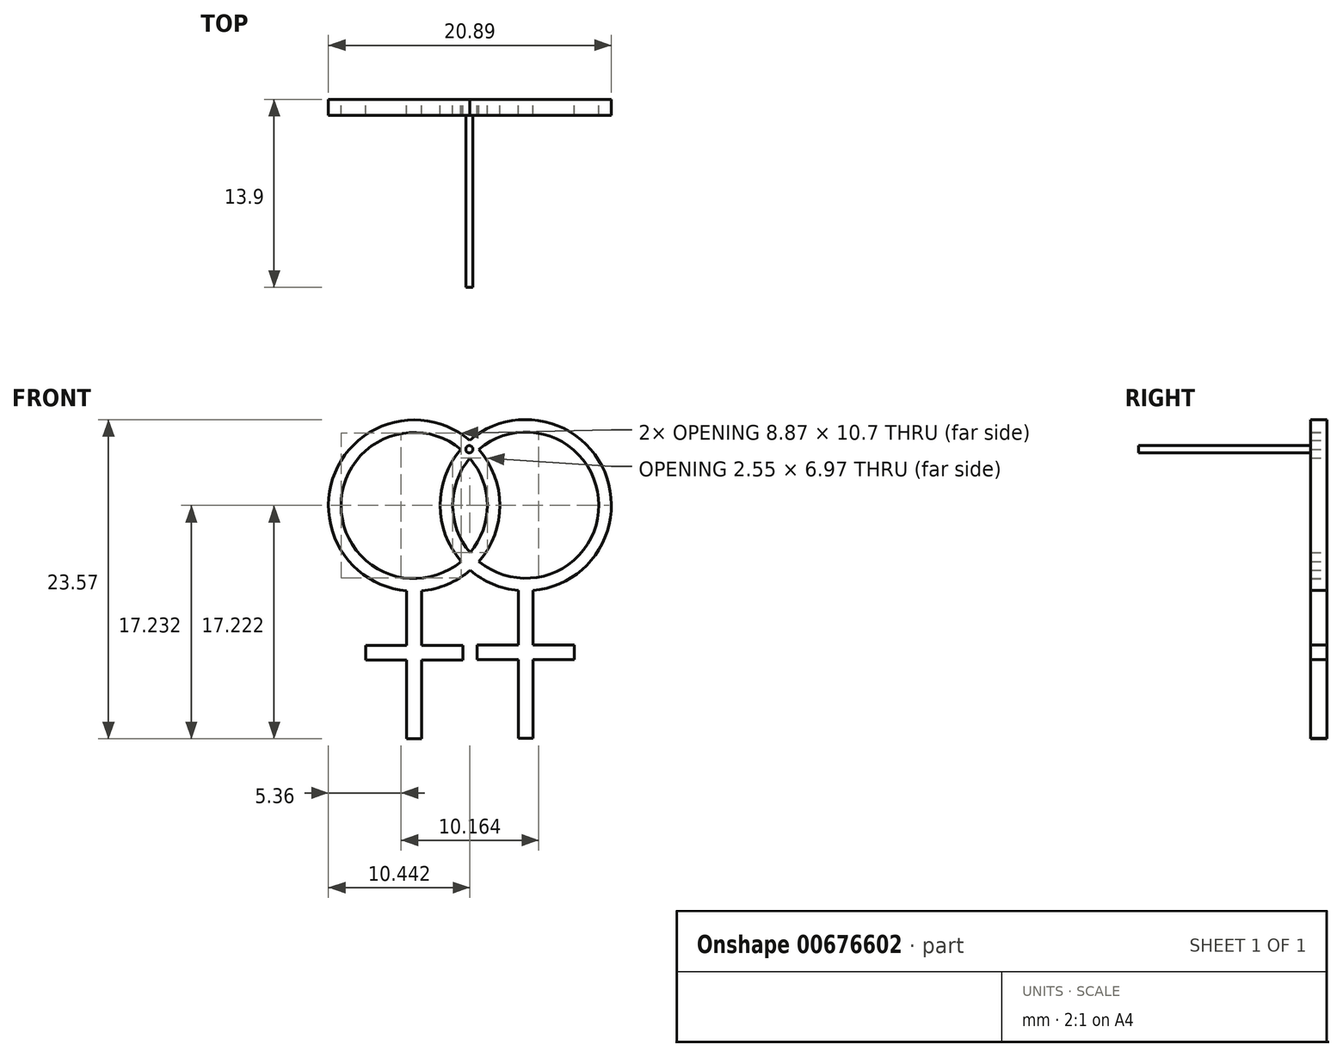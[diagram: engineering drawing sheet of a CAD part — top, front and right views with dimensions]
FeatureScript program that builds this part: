
annotation { "Feature Type Name" : "Feature", "Feature Type Description" : "" }
export const myFeature = defineFeature(function(context is Context, id is Id, definition is map)
    precondition{}
    {
        {
            var Q0;
            Q0=qCreatedBy(makeId("Front.planeOp"),FACE);
            var sketch = newSketch(context, id + "F0", { "sketchPlane" : qUnion([Q0])});
            skArc(sketch, "E0", {"start": v(-22.56, 17.55) * mm, "mid": v(-20.65, 18.03) * mm, "end": v(-18.97, 19.07) * mm});
            skArc(sketch, "E1", {"start": v(-19.66, 28) * mm, "mid": v(-28.5, 23.83) * mm, "end": v(-19.63, 19.72) * mm});
            skLineSegment(sketch, "E2", {"start": v(-23.66, 12.43) * mm, "end": v(-23.66, 6.63) * mm});
            skLineSegment(sketch, "E3", {"start": v(-22.56, 12.43) * mm, "end": v(-22.56, 6.63) * mm});
            skLineSegment(sketch, "E4", {"start": v(-23.66, 6.63) * mm, "end": v(-22.56, 6.63) * mm});
            skPoint(sketch, "E5.orphan", {"position": v(-22.91, 6.63) * mm});
            skPoint(sketch, "E6.start.orphan", {"position": v(-23.1, 30.17) * mm});
            skPoint(sketch, "E7.oppositeSnap0", {"position": v(-22.56, 12.43) * mm});
            skPoint(sketch, "E7.right.end.orphan", {"position": v(-17.65, 12.43) * mm});
            skLineSegment(sketch, "E8", {"start": v(-23.66, 17.55) * mm, "end": v(-23.66, 13.53) * mm});
            skLineSegment(sketch, "E9", {"start": v(-23.66, 13.53) * mm, "end": v(-26.7, 13.53) * mm});
            skLineSegment(sketch, "E10", {"start": v(-26.7, 13.53) * mm, "end": v(-26.7, 12.43) * mm});
            skLineSegment(sketch, "E11", {"start": v(-26.7, 12.43) * mm, "end": v(-23.66, 12.43) * mm});
            skLineSegment(sketch, "E12", {"start": v(-22.56, 17.55) * mm, "end": v(-22.56, 13.53) * mm});
            skLineSegment(sketch, "E13", {"start": v(-22.56, 13.53) * mm, "end": v(-19.52, 13.53) * mm});
            skLineSegment(sketch, "E14", {"start": v(-19.52, 13.53) * mm, "end": v(-19.52, 12.43) * mm});
            skLineSegment(sketch, "E15", {"start": v(-19.52, 12.43) * mm, "end": v(-22.56, 12.43) * mm});
            skArc(sketch, "E16", {"start": v(-14.32, 17.58) * mm, "mid": v(-9.04, 26.34) * mm, "end": v(-19, 28.66) * mm});
            skArc(sketch, "E17", {"start": v(-19, 27.35) * mm, "mid": v(-20.26, 23.86) * mm, "end": v(-18.98, 20.38) * mm});
            skLineSegment(sketch, "E18", {"start": v(-15.42, 12.46) * mm, "end": v(-15.42, 6.66) * mm});
            skLineSegment(sketch, "E19", {"start": v(-14.32, 12.46) * mm, "end": v(-14.32, 6.66) * mm});
            skLineSegment(sketch, "E20", {"start": v(-15.42, 6.66) * mm, "end": v(-14.32, 6.66) * mm});
            skPoint(sketch, "E21.orphan", {"position": v(-14.67, 6.66) * mm});
            skPoint(sketch, "E22.start.orphan", {"position": v(-14.87, 30.2) * mm});
            skPoint(sketch, "E23.oppositeSnap0", {"position": v(-14.32, 12.46) * mm});
            skPoint(sketch, "E23.right.end.orphan", {"position": v(-9.41, 12.46) * mm});
            skLineSegment(sketch, "E24", {"start": v(-15.42, 17.58) * mm, "end": v(-15.42, 13.56) * mm});
            skLineSegment(sketch, "E25", {"start": v(-15.42, 13.56) * mm, "end": v(-18.46, 13.56) * mm});
            skLineSegment(sketch, "E26", {"start": v(-18.46, 13.56) * mm, "end": v(-18.46, 12.46) * mm});
            skLineSegment(sketch, "E27", {"start": v(-18.46, 12.46) * mm, "end": v(-15.42, 12.46) * mm});
            skLineSegment(sketch, "E28", {"start": v(-14.32, 17.58) * mm, "end": v(-14.32, 13.56) * mm});
            skLineSegment(sketch, "E29", {"start": v(-14.32, 13.56) * mm, "end": v(-11.28, 13.56) * mm});
            skLineSegment(sketch, "E30", {"start": v(-11.28, 13.56) * mm, "end": v(-11.28, 12.46) * mm});
            skLineSegment(sketch, "E31", {"start": v(-11.28, 12.46) * mm, "end": v(-14.32, 12.46) * mm});
            skArc(sketch, "E32.trimOffspring", {"start": v(-19, 28.66) * mm, "mid": v(-28.94, 26.3) * mm, "end": v(-23.66, 17.55) * mm});
            skArc(sketch, "E33.trimOffspring", {"start": v(-19.66, 28) * mm, "mid": v(-21.2, 23.86) * mm, "end": v(-19.63, 19.72) * mm});
            skArc(sketch, "E34.trimOffspring", {"start": v(-18.32, 19.72) * mm, "mid": v(-9.47, 23.9) * mm, "end": v(-18.34, 28) * mm});
            skArc(sketch, "E35.trimOffspring", {"start": v(-18.32, 19.72) * mm, "mid": v(-16.79, 23.87) * mm, "end": v(-18.34, 28) * mm});
            skArc(sketch, "E36.trimOffspring", {"start": v(-18.98, 20.38) * mm, "mid": v(-17.71, 23.87) * mm, "end": v(-19, 27.35) * mm});
            skArc(sketch, "E37.trimOffspring", {"start": v(-18.97, 19.07) * mm, "mid": v(-17.31, 18.04) * mm, "end": v(-15.42, 17.58) * mm});
            skSolve(sketch);
        }
        {
            var Q0;
            Q0=makeQuery(id+"F0.imprint","IMPRINT",FACE,{"disambiguationData":[TD([[makeQuery(id+"F0.imprint","IMPRINT",EDGE,{"derivedFrom":sQuery(id+"F0.wireOp",EDGE,"E0")}),1.0]])]});
            extrude(context, id + "F1", {"entities" : qUnion([Q0]), "depth" : 1.2 * mm, "offsetDistance" : 25.4 * mm});
        }
        {
            var Q0;
            Q0=makeQuery(id+"F1.opExtrude","CAP_FACE",FACE,{"disambiguationData":[OSD([sQuery(id+"F0.wireOp",EDGE,"E0"),sQuery(id+"F0.wireOp",EDGE,"E1"),sQuery(id+"F0.wireOp",EDGE,"E2"),sQuery(id+"F0.wireOp",EDGE,"E3"),sQuery(id+"F0.wireOp",EDGE,"E4"),sQuery(id+"F0.wireOp",EDGE,"E8"),sQuery(id+"F0.wireOp",EDGE,"E9"),sQuery(id+"F0.wireOp",EDGE,"E10"),sQuery(id+"F0.wireOp",EDGE,"E11"),sQuery(id+"F0.wireOp",EDGE,"E12"),sQuery(id+"F0.wireOp",EDGE,"E13"),sQuery(id+"F0.wireOp",EDGE,"E14"),sQuery(id+"F0.wireOp",EDGE,"E15"),sQuery(id+"F0.wireOp",EDGE,"E16"),sQuery(id+"F0.wireOp",EDGE,"E17"),sQuery(id+"F0.wireOp",EDGE,"E18"),sQuery(id+"F0.wireOp",EDGE,"E19"),sQuery(id+"F0.wireOp",EDGE,"E20"),sQuery(id+"F0.wireOp",EDGE,"E24"),sQuery(id+"F0.wireOp",EDGE,"E25"),sQuery(id+"F0.wireOp",EDGE,"E26"),sQuery(id+"F0.wireOp",EDGE,"E27"),sQuery(id+"F0.wireOp",EDGE,"E28"),sQuery(id+"F0.wireOp",EDGE,"E29"),sQuery(id+"F0.wireOp",EDGE,"E30"),sQuery(id+"F0.wireOp",EDGE,"E31"),sQuery(id+"F0.wireOp",EDGE,"E32.trimOffspring"),sQuery(id+"F0.wireOp",EDGE,"E33.trimOffspring"),sQuery(id+"F0.wireOp",EDGE,"E34.trimOffspring"),sQuery(id+"F0.wireOp",EDGE,"E35.trimOffspring"),sQuery(id+"F0.wireOp",EDGE,"E36.trimOffspring"),sQuery(id+"F0.wireOp",EDGE,"E37.trimOffspring")])],"isStart":false});
            var sketch = newSketch(context, id + "F2", { "sketchPlane" : qUnion([Q0])});
            skCircle(sketch, "E38", {"center": v(-19.03, 28) * mm, "radius": 0.27 * mm});
            skSolve(sketch);
        }
        {
            var Q0;
            Q0=makeQuery(id+"F2.imprint","IMPRINT",FACE,{"disambiguationData":[TD([[makeQuery(id+"F2.imprint","IMPRINT",EDGE,{"derivedFrom":sQuery(id+"F2.wireOp",EDGE,"E38")}),1.0]])]});
            extrude(context, id + "F3", {"entities" : qUnion([Q0]), "operationType" : NewBodyOperationType.ADD, "depth" : 12.7 * mm, "offsetDistance" : 25.4 * mm});
        }
    });
